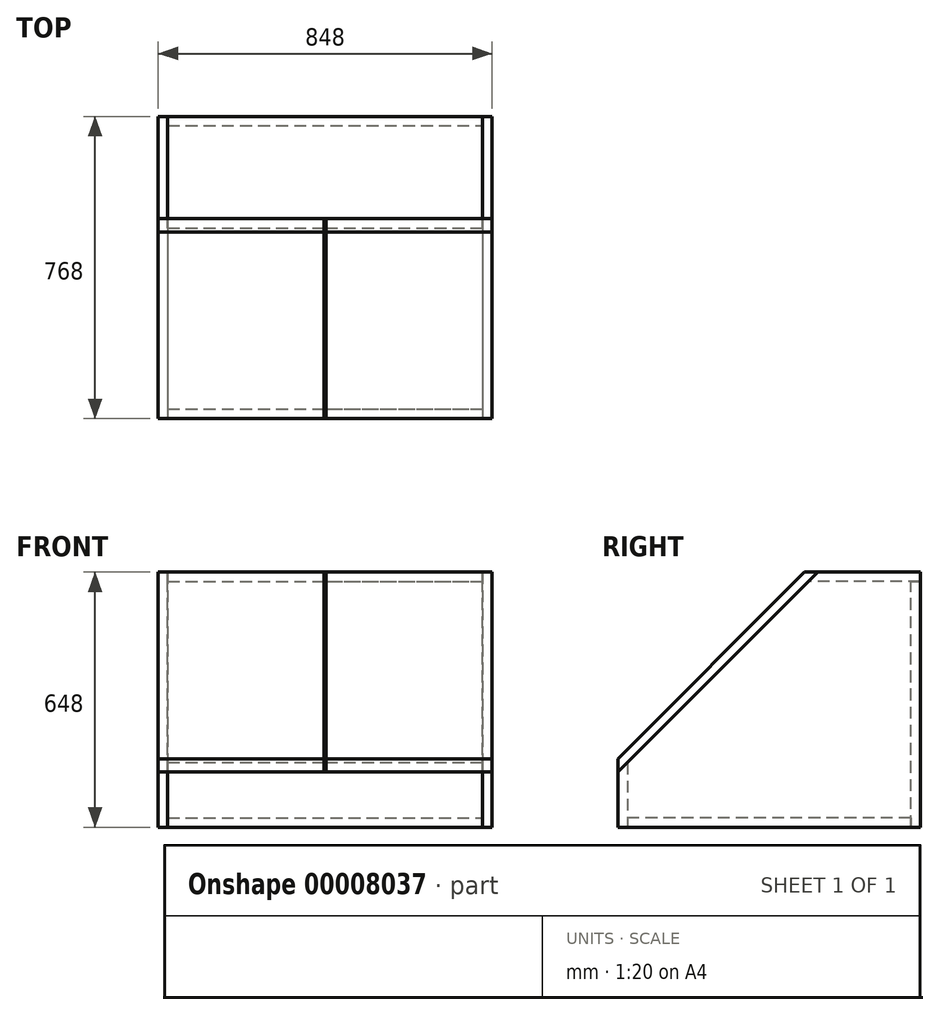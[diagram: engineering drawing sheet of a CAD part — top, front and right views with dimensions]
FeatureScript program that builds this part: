
annotation { "Feature Type Name" : "Feature", "Feature Type Description" : "" }
export const myFeature = defineFeature(function(context is Context, id is Id, definition is map)
    precondition{}
    {
        {
            var Q0;
            Q0=qCreatedBy(makeId("Right.planeOp"),FACE);
            var sketch = newSketch(context, id + "F0", { "sketchPlane" : qUnion([Q0])});
            skLineSegment(sketch, "E0.bottom", {"start": v(0, 0) * mm, "end": v(-720, 0) * mm});
            skLineSegment(sketch, "E0.top", {"start": v(0, 600) * mm, "end": v(-260, 600) * mm});
            skLineSegment(sketch, "E0.left", {"start": v(0, 0) * mm, "end": v(0, 600) * mm});
            skLineSegment(sketch, "E0.right", {"start": v(-720, 0) * mm, "end": v(-720, 140) * mm});
            skLineSegment(sketch, "E1", {"start": v(-720, 140) * mm, "end": v(-260, 600) * mm});
            skLineSegment(sketch, "E2.0", {"start": v(24, -24) * mm, "end": v(-744, -24) * mm});
            skLineSegment(sketch, "E2.1", {"start": v(24, -24) * mm, "end": v(24, 624) * mm});
            skLineSegment(sketch, "E2.2", {"start": v(24, 624) * mm, "end": v(-236, 624) * mm});
            skLineSegment(sketch, "E2.4", {"start": v(-744, -24) * mm, "end": v(-744, 116) * mm});
            skLineSegment(sketch, "E3", {"start": v(-720, 140) * mm, "end": v(-744, 116) * mm});
            skLineSegment(sketch, "E4", {"start": v(-260, 600) * mm, "end": v(-236, 624) * mm});
            skLineSegment(sketch, "E5", {"start": v(-720, 0) * mm, "end": v(-720, -24) * mm});
            skLineSegment(sketch, "E6", {"start": v(0, 600) * mm, "end": v(24, 600) * mm});
            skLineSegment(sketch, "E7", {"start": v(0, 0) * mm, "end": v(0, -24) * mm});
            skSolve(sketch);
        }
        {
            var Q0;
            Q0=makeQuery(id+"F0.imprint","IMPRINT",FACE,{"disambiguationData":[TD([[makeQuery(id+"F0.imprint","IMPRINT",EDGE,{"derivedFrom":sQuery(id+"F0.wireOp",EDGE,"E0.bottom")}),1.0]])]});
            var Q1;
            Q1=makeQuery(id+"F0.imprint","IMPRINT",FACE,{"disambiguationData":[TD([[makeQuery(id+"F0.imprint","IMPRINT",EDGE,{"derivedFrom":sQuery(id+"F0.wireOp",EDGE,"E0.left")}),-1.0]])]});
            var Q2;
            Q2=makeQuery(id+"F0.imprint","IMPRINT",FACE,{"disambiguationData":[TD([[makeQuery(id+"F0.imprint","IMPRINT",EDGE,{"derivedFrom":sQuery(id+"F0.wireOp",EDGE,"E0.right")}),1.0]])]});
            var Q3;
            Q3=makeQuery(id+"F0.imprint","IMPRINT",FACE,{"disambiguationData":[TD([[makeQuery(id+"F0.imprint","IMPRINT",EDGE,{"derivedFrom":sQuery(id+"F0.wireOp",EDGE,"E0.bottom")}),-1.0]])]});
            var Q4;
            Q4=makeQuery(id+"F0.imprint","IMPRINT",FACE,{"disambiguationData":[TD([[makeQuery(id+"F0.imprint","IMPRINT",EDGE,{"derivedFrom":sQuery(id+"F0.wireOp",EDGE,"E0.top")}),-1.0]])]});
            extrude(context, id + "F1", {"entities" : qUnion([Q0, Q1, Q2, Q3, Q4]), "depth" : 24 * mm});
        }
        {
            var Q0;
            Q0=qCreatedBy(makeId("Right.planeOp"),FACE);
            cPlane(context, id + "F2", {"entities" : qUnion([Q0]), "cplaneType" : CPlaneType.OFFSET, "offset" : 400 * mm, "oppositeDirection" : true, "width" : 150 * mm, "height" : 150 * mm});
        }
        {
            var Q0;
            Q0=makeQuery(id+"F1.opExtrude","SWEPT_BODY",BODY,{"disambiguationData":[OSD([sQuery(id+"F0.wireOp",EDGE,"E1"),sQuery(id+"F0.wireOp",EDGE,"E2.0"),sQuery(id+"F0.wireOp",EDGE,"E2.1"),sQuery(id+"F0.wireOp",EDGE,"E2.2"),sQuery(id+"F0.wireOp",EDGE,"E2.4"),sQuery(id+"F0.wireOp",EDGE,"E3"),sQuery(id+"F0.wireOp",EDGE,"E4")])]});
            var Q1;
            Q1=qCreatedBy(id+"F2.planeOp",FACE);
            mirror(context, id + "F3", {"entities" : qUnion([Q0]), "mirrorPlane" : qUnion([Q1])});
        }
        {
            var Q0;
            Q0=makeQuery(id+"F0.imprint","IMPRINT",FACE,{"disambiguationData":[TD([[makeQuery(id+"F0.imprint","IMPRINT",EDGE,{"derivedFrom":sQuery(id+"F0.wireOp",EDGE,"E0.bottom")}),1.0]])]});
            extrude(context, id + "F4", {"entities" : qUnion([Q0]), "endBound" : BoundingType.UP_TO_NEXT, "oppositeDirection" : true, "depth" : 800 * mm});
        }
        {
            var Q0;
            Q0=makeQuery(id+"F0.imprint","IMPRINT",FACE,{"disambiguationData":[TD([[makeQuery(id+"F0.imprint","IMPRINT",EDGE,{"derivedFrom":sQuery(id+"F0.wireOp",EDGE,"E0.left")}),-1.0]])]});
            extrude(context, id + "F5", {"entities" : qUnion([Q0]), "endBound" : BoundingType.UP_TO_NEXT, "oppositeDirection" : true, "depth" : 800 * mm});
        }
        {
            var Q0;
            Q0=makeQuery(id+"F0.imprint","IMPRINT",FACE,{"disambiguationData":[TD([[makeQuery(id+"F0.imprint","IMPRINT",EDGE,{"derivedFrom":sQuery(id+"F0.wireOp",EDGE,"E0.top")}),-1.0]])]});
            extrude(context, id + "F6", {"entities" : qUnion([Q0]), "endBound" : BoundingType.UP_TO_NEXT, "oppositeDirection" : true, "depth" : 800 * mm});
        }
        {
            var Q0;
            Q0=makeQuery(id+"F0.imprint","IMPRINT",FACE,{"disambiguationData":[TD([[makeQuery(id+"F0.imprint","IMPRINT",EDGE,{"derivedFrom":sQuery(id+"F0.wireOp",EDGE,"E0.right")}),1.0]])]});
            extrude(context, id + "F7", {"entities" : qUnion([Q0]), "endBound" : BoundingType.UP_TO_NEXT, "oppositeDirection" : true, "depth" : 800 * mm});
        }
        {
            var Q0;
            Q0=makeQuery(id+"F3.opPattern","COPY",FACE,{"derivedFrom":makeQuery(id+"F1.opExtrude","SWEPT_FACE",FACE,{"disambiguationData":[OSD([sQuery(id+"F0.wireOp",EDGE,"E1"),sQuery(id+"F0.wireOp",EDGE,"E3"),sQuery(id+"F0.wireOp",EDGE,"E4")])]}),"instanceName":"1"});
            var sketch = newSketch(context, id + "F8", { "sketchPlane" : qUnion([Q0])});
            skLineSegment(sketch, "E8.bottom", {"start": v(-824, 274.36) * mm, "end": v(-402, 274.36) * mm});
            skLineSegment(sketch, "E8.top", {"start": v(-824, -444.06) * mm, "end": v(-402, -444.06) * mm});
            skLineSegment(sketch, "E8.left", {"start": v(-824, 274.36) * mm, "end": v(-824, -444.06) * mm});
            skLineSegment(sketch, "E8.right", {"start": v(-402, 274.36) * mm, "end": v(-402, -444.06) * mm});
            skSolve(sketch);
        }
        {
            var Q0;
            {var subQ1=sQuery(id+"F8.wireOp",EDGE,"E8.left");Q0=makeQuery(id+"F8.imprint","IMPRINT",FACE,{"disambiguationData":[TD([[makeQuery(id+"F8.imprint","IMPRINT",EDGE,{"derivedFrom":subQ1}),1.0]])]});}
            var Q1;
            {var subQ1=sQuery(id+"F8.wireOp",EDGE,"E8.right");Q1=makeQuery(id+"F8.imprint","IMPRINT",FACE,{"disambiguationData":[TD([[makeQuery(id+"F8.imprint","IMPRINT",EDGE,{"derivedFrom":subQ1}),-1.0]])]});}
            extrude(context, id + "F9", {"entities" : qUnion([Q0, Q1]), "depth" : 24 * mm});
        }
        {
            var Q0;
            Q0=makeQuery(id+"F9.opExtrude","CAP_EDGE",EDGE,{"disambiguationData":[OSD([sQuery(id+"F8.wireOp",EDGE,"E8.bottom")])],"isStart":false});
            var Q1;
            Q1=makeQuery(id+"F9.opExtrude","CAP_EDGE",EDGE,{"disambiguationData":[OSD([sQuery(id+"F8.wireOp",EDGE,"E8.top")])],"isStart":false});
            chamfer(context, id + "F10", {"entities" : qUnion([Q0, Q1]), "width" : 24 * mm, "tangentPropagation" : true});
        }
        {
            var Q0;
            Q0=makeQuery(id+"F9.opExtrude","SWEPT_BODY",BODY,{"disambiguationData":[OSD([sQuery(id+"F8.wireOp",EDGE,"E8.bottom"),sQuery(id+"F8.wireOp",EDGE,"E8.top"),sQuery(id+"F8.wireOp",EDGE,"E8.left"),sQuery(id+"F8.wireOp",EDGE,"E8.right")])]});
            var Q1;
            Q1=qCreatedBy(id+"F2.planeOp",FACE);
            mirror(context, id + "F11", {"entities" : qUnion([Q0]), "mirrorPlane" : qUnion([Q1])});
        }
    });
